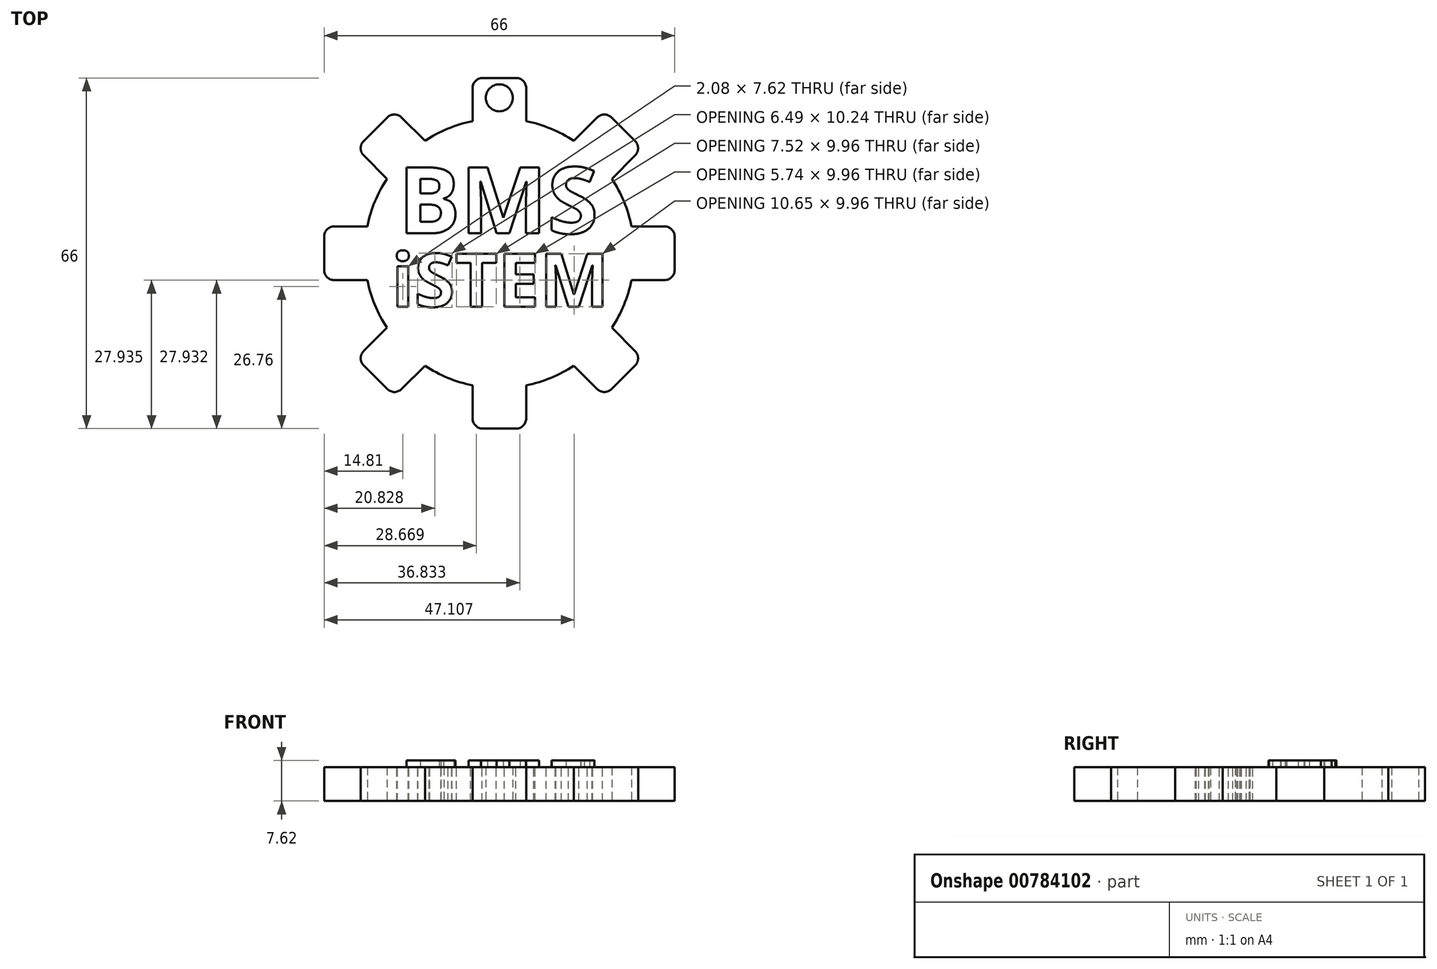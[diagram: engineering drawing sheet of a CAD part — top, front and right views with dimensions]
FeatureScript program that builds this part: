
annotation { "Feature Type Name" : "Feature", "Feature Type Description" : "" }
export const myFeature = defineFeature(function(context is Context, id is Id, definition is map)
    precondition{}
    {
        {
            var Q0;
            Q0=qCreatedBy(makeId("Top.planeOp"),FACE);
            var sketch = newSketch(context, id + "F0", { "sketchPlane" : qUnion([Q0])});
            skCircle(sketch, "E0", {"center": v(0, 0) * mm, "radius": 25.38 * mm});
            skCircle(sketch, "E1.cCircle", {"center": v(0, 0) * mm, "radius": 25.38 * mm, "construction": true});
            skLineSegment(sketch, "E1.0", {"start": v(-5.05, 25.38) * mm, "end": v(5.05, 25.38) * mm});
            skLineSegment(sketch, "E1.1", {"start": v(5.05, 25.38) * mm, "end": v(14.38, 21.52) * mm});
            skLineSegment(sketch, "E1.2", {"start": v(14.38, 21.52) * mm, "end": v(21.52, 14.38) * mm});
            skLineSegment(sketch, "E1.3", {"start": v(21.52, 14.38) * mm, "end": v(25.38, 5.05) * mm});
            skLineSegment(sketch, "E1.4", {"start": v(25.38, 5.05) * mm, "end": v(25.38, -5.05) * mm});
            skLineSegment(sketch, "E1.5", {"start": v(25.38, -5.05) * mm, "end": v(21.52, -14.38) * mm});
            skLineSegment(sketch, "E1.6", {"start": v(21.52, -14.38) * mm, "end": v(14.38, -21.52) * mm});
            skLineSegment(sketch, "E1.7", {"start": v(14.38, -21.52) * mm, "end": v(5.05, -25.38) * mm});
            skLineSegment(sketch, "E1.8", {"start": v(5.05, -25.38) * mm, "end": v(-5.05, -25.38) * mm});
            skLineSegment(sketch, "E1.9", {"start": v(-5.05, -25.38) * mm, "end": v(-14.38, -21.52) * mm});
            skLineSegment(sketch, "E1.10", {"start": v(-14.38, -21.52) * mm, "end": v(-21.52, -14.38) * mm});
            skLineSegment(sketch, "E1.11", {"start": v(-21.52, -14.38) * mm, "end": v(-25.38, -5.05) * mm});
            skLineSegment(sketch, "E1.12", {"start": v(-25.38, -5.05) * mm, "end": v(-25.38, 5.05) * mm});
            skLineSegment(sketch, "E1.13", {"start": v(-25.38, 5.05) * mm, "end": v(-21.52, 14.38) * mm});
            skLineSegment(sketch, "E1.14", {"start": v(-21.52, 14.38) * mm, "end": v(-14.38, 21.52) * mm});
            skLineSegment(sketch, "E1.15", {"start": v(-14.38, 21.52) * mm, "end": v(-5.05, 25.38) * mm});
            skPoint(sketch, "E1.0.midPoint", {"position": v(0, 25.38) * mm});
            skLineSegment(sketch, "E2", {"start": v(-5.05, 25.38) * mm, "end": v(-5.05, 31.1) * mm});
            skLineSegment(sketch, "E3", {"start": v(-3.14, 33) * mm, "end": v(3.14, 33) * mm});
            skLineSegment(sketch, "E4", {"start": v(5.05, 31.1) * mm, "end": v(5.05, 25.38) * mm});
            skLineSegment(sketch, "E5", {"start": v(14.38, 21.52) * mm, "end": v(18.42, 25.56) * mm});
            skLineSegment(sketch, "E6", {"start": v(21.52, 14.38) * mm, "end": v(25.56, 18.42) * mm});
            skLineSegment(sketch, "E7", {"start": v(21.11, 25.56) * mm, "end": v(25.56, 21.11) * mm});
            skLineSegment(sketch, "E8", {"start": v(-14.38, 21.52) * mm, "end": v(-18.42, 25.56) * mm});
            skLineSegment(sketch, "E9", {"start": v(-21.52, 14.38) * mm, "end": v(-25.56, 18.42) * mm});
            skLineSegment(sketch, "E10", {"start": v(-25.56, 21.11) * mm, "end": v(-21.11, 25.56) * mm});
            skLineSegment(sketch, "E11", {"start": v(-25.38, 5.05) * mm, "end": v(-31.1, 5.05) * mm});
            skLineSegment(sketch, "E12", {"start": v(-33, 3.14) * mm, "end": v(-33, -3.14) * mm});
            skLineSegment(sketch, "E13", {"start": v(-31.1, -5.05) * mm, "end": v(-25.38, -5.05) * mm});
            skLineSegment(sketch, "E14", {"start": v(-21.52, -14.38) * mm, "end": v(-25.56, -18.42) * mm});
            skLineSegment(sketch, "E15", {"start": v(-14.38, -21.52) * mm, "end": v(-18.42, -25.56) * mm});
            skLineSegment(sketch, "E16", {"start": v(-21.1, -25.56) * mm, "end": v(-25.56, -21.11) * mm});
            skLineSegment(sketch, "E17", {"start": v(-5.05, -25.38) * mm, "end": v(-5.05, -31.1) * mm});
            skLineSegment(sketch, "E18", {"start": v(-3.14, -33) * mm, "end": v(3.14, -33) * mm});
            skLineSegment(sketch, "E19", {"start": v(5.05, -31.1) * mm, "end": v(5.05, -25.38) * mm});
            skLineSegment(sketch, "E20", {"start": v(14.38, -21.52) * mm, "end": v(18.42, -25.56) * mm});
            skLineSegment(sketch, "E21", {"start": v(21.52, -14.38) * mm, "end": v(25.56, -18.42) * mm});
            skLineSegment(sketch, "E22", {"start": v(25.56, -21.11) * mm, "end": v(21.11, -25.56) * mm});
            skLineSegment(sketch, "E23", {"start": v(25.38, 5.05) * mm, "end": v(31.1, 5.05) * mm});
            skLineSegment(sketch, "E24", {"start": v(25.38, -5.05) * mm, "end": v(31.1, -5.05) * mm});
            skLineSegment(sketch, "E25", {"start": v(33, -3.14) * mm, "end": v(33, 3.14) * mm});
            skPoint(sketch, "E26.visualSharp", {"position": v(-19.77, 26.9) * mm});
            skArc(sketch, "E26.filletArc", {"start": v(-18.42, 25.56) * mm, "mid": v(-19.77, 26.12) * mm, "end": v(-21.11, 25.56) * mm});
            skPoint(sketch, "E27.visualSharp", {"position": v(-26.9, 19.77) * mm});
            skArc(sketch, "E27.filletArc", {"start": v(-25.56, 21.11) * mm, "mid": v(-26.12, 19.77) * mm, "end": v(-25.56, 18.42) * mm});
            skPoint(sketch, "E28.visualSharp", {"position": v(-33, 5.05) * mm});
            skArc(sketch, "E28.filletArc", {"start": v(-31.1, 5.05) * mm, "mid": v(-32.45, 4.5) * mm, "end": v(-33, 3.14) * mm});
            skPoint(sketch, "E29.visualSharp", {"position": v(-33, -5.05) * mm});
            skArc(sketch, "E29.filletArc", {"start": v(-33, -3.14) * mm, "mid": v(-32.45, -4.5) * mm, "end": v(-31.1, -5.05) * mm});
            skPoint(sketch, "E30.visualSharp", {"position": v(-26.9, -19.77) * mm});
            skArc(sketch, "E30.filletArc", {"start": v(-25.56, -18.42) * mm, "mid": v(-26.12, -19.77) * mm, "end": v(-25.56, -21.11) * mm});
            skPoint(sketch, "E31.visualSharp", {"position": v(-19.76, -26.9) * mm});
            skArc(sketch, "E31.filletArc", {"start": v(-21.1, -25.56) * mm, "mid": v(-19.76, -26.11) * mm, "end": v(-18.42, -25.56) * mm});
            skPoint(sketch, "E32.visualSharp", {"position": v(5.05, -33) * mm});
            skArc(sketch, "E32.filletArc", {"start": v(3.14, -33) * mm, "mid": v(4.5, -32.45) * mm, "end": v(5.05, -31.1) * mm});
            skPoint(sketch, "E33.visualSharp", {"position": v(-5.05, -33) * mm});
            skArc(sketch, "E33.filletArc", {"start": v(-5.05, -31.1) * mm, "mid": v(-4.5, -32.45) * mm, "end": v(-3.14, -33) * mm});
            skPoint(sketch, "E34.visualSharp", {"position": v(19.77, -26.9) * mm});
            skArc(sketch, "E34.filletArc", {"start": v(18.42, -25.56) * mm, "mid": v(19.77, -26.12) * mm, "end": v(21.11, -25.56) * mm});
            skPoint(sketch, "E35.visualSharp", {"position": v(26.9, -19.77) * mm});
            skArc(sketch, "E35.filletArc", {"start": v(25.56, -21.11) * mm, "mid": v(26.12, -19.77) * mm, "end": v(25.56, -18.42) * mm});
            skPoint(sketch, "E36.visualSharp", {"position": v(33, -5.05) * mm});
            skArc(sketch, "E36.filletArc", {"start": v(31.1, -5.05) * mm, "mid": v(32.45, -4.5) * mm, "end": v(33, -3.14) * mm});
            skPoint(sketch, "E37.visualSharp", {"position": v(33, 5.05) * mm});
            skArc(sketch, "E37.filletArc", {"start": v(33, 3.14) * mm, "mid": v(32.45, 4.5) * mm, "end": v(31.1, 5.05) * mm});
            skPoint(sketch, "E38.visualSharp", {"position": v(26.9, 19.77) * mm});
            skArc(sketch, "E38.filletArc", {"start": v(25.56, 18.42) * mm, "mid": v(26.12, 19.77) * mm, "end": v(25.56, 21.11) * mm});
            skPoint(sketch, "E39.visualSharp", {"position": v(19.77, 26.9) * mm});
            skArc(sketch, "E39.filletArc", {"start": v(21.11, 25.56) * mm, "mid": v(19.77, 26.12) * mm, "end": v(18.42, 25.56) * mm});
            skPoint(sketch, "E40.visualSharp", {"position": v(5.05, 33) * mm});
            skArc(sketch, "E40.filletArc", {"start": v(5.05, 31.1) * mm, "mid": v(4.5, 32.45) * mm, "end": v(3.14, 33) * mm});
            skPoint(sketch, "E41.visualSharp", {"position": v(-5.05, 33) * mm});
            skArc(sketch, "E41.filletArc", {"start": v(-3.14, 33) * mm, "mid": v(-4.5, 32.45) * mm, "end": v(-5.05, 31.1) * mm});
            skLineSegment(sketch, "E42", {"start": v(-5.05, 25.38) * mm, "end": v(-5.05, 24.88) * mm});
            skLineSegment(sketch, "E43", {"start": v(5.05, 25.38) * mm, "end": v(5.05, 24.88) * mm});
            skLineSegment(sketch, "E44", {"start": v(14.38, 21.52) * mm, "end": v(14.02, 21.16) * mm});
            skLineSegment(sketch, "E45", {"start": v(21.52, 14.38) * mm, "end": v(21.16, 14.02) * mm});
            skLineSegment(sketch, "E46", {"start": v(25.38, 5.05) * mm, "end": v(24.88, 5.05) * mm});
            skLineSegment(sketch, "E47", {"start": v(25.38, -5.05) * mm, "end": v(24.88, -5.05) * mm});
            skLineSegment(sketch, "E48", {"start": v(21.52, -14.38) * mm, "end": v(21.16, -14.02) * mm});
            skLineSegment(sketch, "E49", {"start": v(14.38, -21.52) * mm, "end": v(14.02, -21.16) * mm});
            skLineSegment(sketch, "E50", {"start": v(5.05, -25.38) * mm, "end": v(5.05, -24.88) * mm});
            skLineSegment(sketch, "E51", {"start": v(-5.05, -25.38) * mm, "end": v(-5.05, -24.88) * mm});
            skLineSegment(sketch, "E52", {"start": v(-14.38, -21.52) * mm, "end": v(-14.02, -21.16) * mm});
            skLineSegment(sketch, "E53", {"start": v(-21.52, -14.38) * mm, "end": v(-21.16, -14.02) * mm});
            skLineSegment(sketch, "E54", {"start": v(-25.38, -5.05) * mm, "end": v(-24.88, -5.05) * mm});
            skLineSegment(sketch, "E55", {"start": v(-25.38, 5.05) * mm, "end": v(-24.88, 5.05) * mm});
            skLineSegment(sketch, "E56", {"start": v(-21.52, 14.38) * mm, "end": v(-21.16, 14.02) * mm});
            skLineSegment(sketch, "E57", {"start": v(-14.38, 21.52) * mm, "end": v(-14.02, 21.16) * mm});
            skCircle(sketch, "E58", {"center": v(0, 29.27) * mm, "radius": 2.54 * mm});
            skSolve(sketch);
        }
        {
            var Q0;
            {var subQ3=sQuery(id+"F0.wireOp",EDGE,"E8");Q0=makeQuery(id+"F0.imprint","IMPRINT",FACE,{"disambiguationData":[TD([[makeQuery(id+"F0.imprint","IMPRINT",EDGE,{"derivedFrom":subQ3}),1.0]])]});}
            var Q1;
            {var subQ0=sQuery(id+"F0.wireOp",EDGE,"E2");Q1=makeQuery(id+"F0.imprint","IMPRINT",FACE,{"disambiguationData":[TD([[makeQuery(id+"F0.imprint","IMPRINT",EDGE,{"derivedFrom":subQ0}),-1.0]])]});}
            var Q2;
            {var subQ1=sQuery(id+"F0.wireOp",EDGE,"E5");Q2=makeQuery(id+"F0.imprint","IMPRINT",FACE,{"disambiguationData":[TD([[makeQuery(id+"F0.imprint","IMPRINT",EDGE,{"derivedFrom":subQ1}),-1.0]])]});}
            var Q3;
            {var subQ3=sQuery(id+"F0.wireOp",EDGE,"E23");Q3=makeQuery(id+"F0.imprint","IMPRINT",FACE,{"disambiguationData":[TD([[makeQuery(id+"F0.imprint","IMPRINT",EDGE,{"derivedFrom":subQ3}),-1.0]])]});}
            var Q4;
            {var subQ1=sQuery(id+"F0.wireOp",EDGE,"E20");Q4=makeQuery(id+"F0.imprint","IMPRINT",FACE,{"disambiguationData":[TD([[makeQuery(id+"F0.imprint","IMPRINT",EDGE,{"derivedFrom":subQ1}),1.0]])]});}
            var Q5;
            {var subQ0=sQuery(id+"F0.wireOp",EDGE,"E17");Q5=makeQuery(id+"F0.imprint","IMPRINT",FACE,{"disambiguationData":[TD([[makeQuery(id+"F0.imprint","IMPRINT",EDGE,{"derivedFrom":subQ0}),1.0]])]});}
            var Q6;
            {var subQ0=sQuery(id+"F0.wireOp",EDGE,"E14");Q6=makeQuery(id+"F0.imprint","IMPRINT",FACE,{"disambiguationData":[TD([[makeQuery(id+"F0.imprint","IMPRINT",EDGE,{"derivedFrom":subQ0}),1.0]])]});}
            var Q7;
            {var subQ0=sQuery(id+"F0.wireOp",EDGE,"E11");Q7=makeQuery(id+"F0.imprint","IMPRINT",FACE,{"disambiguationData":[TD([[makeQuery(id+"F0.imprint","IMPRINT",EDGE,{"derivedFrom":subQ0}),1.0]])]});}
            var Q8;
            {var subQ0=sQuery(id+"F0.wireOp",EDGE,"E42");Q8=makeQuery(id+"F0.imprint","IMPRINT",FACE,{"disambiguationData":[TD([[makeQuery(id+"F0.imprint","IMPRINT",EDGE,{"derivedFrom":subQ0}),1.0]])]});}
            var Q9;
            {var subQ0=sQuery(id+"F0.wireOp",EDGE,"E43");Q9=makeQuery(id+"F0.imprint","IMPRINT",FACE,{"disambiguationData":[TD([[makeQuery(id+"F0.imprint","IMPRINT",EDGE,{"derivedFrom":subQ0}),-1.0]])]});}
            var Q10;
            {var subQ0=sQuery(id+"F0.wireOp",EDGE,"E44");Q10=makeQuery(id+"F0.imprint","IMPRINT",FACE,{"disambiguationData":[TD([[makeQuery(id+"F0.imprint","IMPRINT",EDGE,{"derivedFrom":subQ0}),1.0]])]});}
            var Q11;
            {var subQ0=sQuery(id+"F0.wireOp",EDGE,"E45");Q11=makeQuery(id+"F0.imprint","IMPRINT",FACE,{"disambiguationData":[TD([[makeQuery(id+"F0.imprint","IMPRINT",EDGE,{"derivedFrom":subQ0}),-1.0]])]});}
            var Q12;
            {var subQ0=sQuery(id+"F0.wireOp",EDGE,"E46");Q12=makeQuery(id+"F0.imprint","IMPRINT",FACE,{"disambiguationData":[TD([[makeQuery(id+"F0.imprint","IMPRINT",EDGE,{"derivedFrom":subQ0}),1.0]])]});}
            var Q13;
            {var subQ0=sQuery(id+"F0.wireOp",EDGE,"E47");Q13=makeQuery(id+"F0.imprint","IMPRINT",FACE,{"disambiguationData":[TD([[makeQuery(id+"F0.imprint","IMPRINT",EDGE,{"derivedFrom":subQ0}),-1.0]])]});}
            var Q14;
            {var subQ0=sQuery(id+"F0.wireOp",EDGE,"E48");Q14=makeQuery(id+"F0.imprint","IMPRINT",FACE,{"disambiguationData":[TD([[makeQuery(id+"F0.imprint","IMPRINT",EDGE,{"derivedFrom":subQ0}),1.0]])]});}
            var Q15;
            {var subQ0=sQuery(id+"F0.wireOp",EDGE,"E49");Q15=makeQuery(id+"F0.imprint","IMPRINT",FACE,{"disambiguationData":[TD([[makeQuery(id+"F0.imprint","IMPRINT",EDGE,{"derivedFrom":subQ0}),-1.0]])]});}
            var Q16;
            {var subQ0=sQuery(id+"F0.wireOp",EDGE,"E51");Q16=makeQuery(id+"F0.imprint","IMPRINT",FACE,{"disambiguationData":[TD([[makeQuery(id+"F0.imprint","IMPRINT",EDGE,{"derivedFrom":subQ0}),-1.0]])]});}
            var Q17;
            {var subQ0=sQuery(id+"F0.wireOp",EDGE,"E50");Q17=makeQuery(id+"F0.imprint","IMPRINT",FACE,{"disambiguationData":[TD([[makeQuery(id+"F0.imprint","IMPRINT",EDGE,{"derivedFrom":subQ0}),1.0]])]});}
            var Q18;
            {var subQ0=sQuery(id+"F0.wireOp",EDGE,"E0");var subQ17=makeQuery(id+"F0.imprint","INTERSECT",VERTEX,{"derivedFrom":[subQ0,sQuery(id+"F0.wireOp",EDGE,"E46")]});Q18=makeQuery(id+"F0.imprint","IMPRINT",FACE,{"disambiguationData":[TD([[makeQuery(id+"F0.imprint","IMPRINT",EDGE,{"disambiguationData":[TD([[subQ17,1.0]])],"derivedFrom":subQ0}),1.0]])]});}
            var Q19;
            {var subQ0=sQuery(id+"F0.wireOp",EDGE,"E52");Q19=makeQuery(id+"F0.imprint","IMPRINT",FACE,{"disambiguationData":[TD([[makeQuery(id+"F0.imprint","IMPRINT",EDGE,{"derivedFrom":subQ0}),1.0]])]});}
            var Q20;
            {var subQ0=sQuery(id+"F0.wireOp",EDGE,"E53");Q20=makeQuery(id+"F0.imprint","IMPRINT",FACE,{"disambiguationData":[TD([[makeQuery(id+"F0.imprint","IMPRINT",EDGE,{"derivedFrom":subQ0}),-1.0]])]});}
            var Q21;
            {var subQ0=sQuery(id+"F0.wireOp",EDGE,"E54");Q21=makeQuery(id+"F0.imprint","IMPRINT",FACE,{"disambiguationData":[TD([[makeQuery(id+"F0.imprint","IMPRINT",EDGE,{"derivedFrom":subQ0}),1.0]])]});}
            var Q22;
            {var subQ0=sQuery(id+"F0.wireOp",EDGE,"E55");Q22=makeQuery(id+"F0.imprint","IMPRINT",FACE,{"disambiguationData":[TD([[makeQuery(id+"F0.imprint","IMPRINT",EDGE,{"derivedFrom":subQ0}),-1.0]])]});}
            var Q23;
            {var subQ0=sQuery(id+"F0.wireOp",EDGE,"E56");Q23=makeQuery(id+"F0.imprint","IMPRINT",FACE,{"disambiguationData":[TD([[makeQuery(id+"F0.imprint","IMPRINT",EDGE,{"derivedFrom":subQ0}),1.0]])]});}
            var Q24;
            {var subQ0=sQuery(id+"F0.wireOp",EDGE,"E57");Q24=makeQuery(id+"F0.imprint","IMPRINT",FACE,{"disambiguationData":[TD([[makeQuery(id+"F0.imprint","IMPRINT",EDGE,{"derivedFrom":subQ0}),-1.0]])]});}
            extrude(context, id + "F1", {"entities" : qUnion([Q0, Q1, Q2, Q3, Q4, Q5, Q6, Q7, Q8, Q9, Q10, Q11, Q12, Q13, Q14, Q15, Q16, Q17, Q18, Q19, Q20, Q21, Q22, Q23, Q24]), "depth" : 6.35 * mm, "offsetDistance" : 25.4 * mm});
        }
        {
            var Q0;
            Q0=makeQuery(id+"F1.opExtrude","CAP_FACE",FACE,{"disambiguationData":[OSD([sQuery(id+"F0.wireOp",EDGE,"E1.1"),sQuery(id+"F0.wireOp",EDGE,"E1.3"),sQuery(id+"F0.wireOp",EDGE,"E1.5"),sQuery(id+"F0.wireOp",EDGE,"E1.7"),sQuery(id+"F0.wireOp",EDGE,"E1.9"),sQuery(id+"F0.wireOp",EDGE,"E1.11"),sQuery(id+"F0.wireOp",EDGE,"E1.13"),sQuery(id+"F0.wireOp",EDGE,"E1.15"),sQuery(id+"F0.wireOp",EDGE,"E2"),sQuery(id+"F0.wireOp",EDGE,"E3"),sQuery(id+"F0.wireOp",EDGE,"E4"),sQuery(id+"F0.wireOp",EDGE,"E5"),sQuery(id+"F0.wireOp",EDGE,"E6"),sQuery(id+"F0.wireOp",EDGE,"E7"),sQuery(id+"F0.wireOp",EDGE,"E8"),sQuery(id+"F0.wireOp",EDGE,"E9"),sQuery(id+"F0.wireOp",EDGE,"E10"),sQuery(id+"F0.wireOp",EDGE,"E11"),sQuery(id+"F0.wireOp",EDGE,"E12"),sQuery(id+"F0.wireOp",EDGE,"E13"),sQuery(id+"F0.wireOp",EDGE,"E14"),sQuery(id+"F0.wireOp",EDGE,"E15"),sQuery(id+"F0.wireOp",EDGE,"E16"),sQuery(id+"F0.wireOp",EDGE,"E17"),sQuery(id+"F0.wireOp",EDGE,"E18"),sQuery(id+"F0.wireOp",EDGE,"E19"),sQuery(id+"F0.wireOp",EDGE,"E20"),sQuery(id+"F0.wireOp",EDGE,"E21"),sQuery(id+"F0.wireOp",EDGE,"E22"),sQuery(id+"F0.wireOp",EDGE,"E23"),sQuery(id+"F0.wireOp",EDGE,"E24"),sQuery(id+"F0.wireOp",EDGE,"E25")])],"isStart":false});
            var sketch = newSketch(context, id + "F2", { "sketchPlane" : qUnion([Q0])});
            skText(sketch, "E59", { "text": "iSTEM", "fontName": "OpenSans-Bold.ttf"});
            const initialGuessF2  = {"E59": [-0.02032, -0.01005, 1, 0, 0.01005]};
            skSetInitialGuess(sketch, initialGuessF2);
            skSolve(sketch);
        }
        {
            var Q0;
            Q0 = qSketchRegion(id + "F2", true);
            var Q1;
            Q1=makeQuery(id+"F6ugocPZYVqLwCi_1.imprint","IMPRINT",FACE,{"disambiguationData":[TD([[makeQuery(id+"F6ugocPZYVqLwCi_1.imprint","IMPRINT",EDGE,{"derivedFrom":makeQuery(id+"F2.imprint","IMPRINT",EDGE,{"derivedFrom":sQuery(id+"F2.wireOp",EDGE,"238f4873-60e4-4737-845d-4de3b97efb3e.sketch_text.stroke-32")})}),-1.0]])]});
            extrude(context, id + "F3", {"entities" : qUnion([Q0, Q1]), "operationType" : NewBodyOperationType.REMOVE, "oppositeDirection" : true, "depth" : 42.93 * mm, "offsetDistance" : 25.4 * mm});
        }
        {
            var Q0;
            Q0=makeQuery(id+"F1.opExtrude","CAP_FACE",FACE,{"disambiguationData":[OSD([sQuery(id+"F0.wireOp",EDGE,"E0"),sQuery(id+"F0.wireOp",EDGE,"E2"),sQuery(id+"F0.wireOp",EDGE,"E3"),sQuery(id+"F0.wireOp",EDGE,"E4"),sQuery(id+"F0.wireOp",EDGE,"E5"),sQuery(id+"F0.wireOp",EDGE,"E6"),sQuery(id+"F0.wireOp",EDGE,"E7"),sQuery(id+"F0.wireOp",EDGE,"E8"),sQuery(id+"F0.wireOp",EDGE,"E9"),sQuery(id+"F0.wireOp",EDGE,"E10"),sQuery(id+"F0.wireOp",EDGE,"E11"),sQuery(id+"F0.wireOp",EDGE,"E12"),sQuery(id+"F0.wireOp",EDGE,"E13"),sQuery(id+"F0.wireOp",EDGE,"E14"),sQuery(id+"F0.wireOp",EDGE,"E15"),sQuery(id+"F0.wireOp",EDGE,"E16"),sQuery(id+"F0.wireOp",EDGE,"E17"),sQuery(id+"F0.wireOp",EDGE,"E18"),sQuery(id+"F0.wireOp",EDGE,"E19"),sQuery(id+"F0.wireOp",EDGE,"E20"),sQuery(id+"F0.wireOp",EDGE,"E21"),sQuery(id+"F0.wireOp",EDGE,"E22"),sQuery(id+"F0.wireOp",EDGE,"E23"),sQuery(id+"F0.wireOp",EDGE,"E24"),sQuery(id+"F0.wireOp",EDGE,"E25"),sQuery(id+"F0.wireOp",EDGE,"E26.filletArc"),sQuery(id+"F0.wireOp",EDGE,"E27.filletArc"),sQuery(id+"F0.wireOp",EDGE,"E28.filletArc"),sQuery(id+"F0.wireOp",EDGE,"E29.filletArc"),sQuery(id+"F0.wireOp",EDGE,"E30.filletArc"),sQuery(id+"F0.wireOp",EDGE,"E31.filletArc"),sQuery(id+"F0.wireOp",EDGE,"E32.filletArc"),sQuery(id+"F0.wireOp",EDGE,"E33.filletArc"),sQuery(id+"F0.wireOp",EDGE,"E34.filletArc"),sQuery(id+"F0.wireOp",EDGE,"E35.filletArc"),sQuery(id+"F0.wireOp",EDGE,"E36.filletArc"),sQuery(id+"F0.wireOp",EDGE,"E37.filletArc"),sQuery(id+"F0.wireOp",EDGE,"E38.filletArc"),sQuery(id+"F0.wireOp",EDGE,"E39.filletArc"),sQuery(id+"F0.wireOp",EDGE,"E40.filletArc"),sQuery(id+"F0.wireOp",EDGE,"E41.filletArc"),sQuery(id+"F0.wireOp",EDGE,"E42"),sQuery(id+"F0.wireOp",EDGE,"E43"),sQuery(id+"F0.wireOp",EDGE,"E44"),sQuery(id+"F0.wireOp",EDGE,"E45"),sQuery(id+"F0.wireOp",EDGE,"E46"),sQuery(id+"F0.wireOp",EDGE,"E47"),sQuery(id+"F0.wireOp",EDGE,"E48"),sQuery(id+"F0.wireOp",EDGE,"E49"),sQuery(id+"F0.wireOp",EDGE,"E50"),sQuery(id+"F0.wireOp",EDGE,"E51"),sQuery(id+"F0.wireOp",EDGE,"E52"),sQuery(id+"F0.wireOp",EDGE,"E53"),sQuery(id+"F0.wireOp",EDGE,"E54"),sQuery(id+"F0.wireOp",EDGE,"E55"),sQuery(id+"F0.wireOp",EDGE,"E56"),sQuery(id+"F0.wireOp",EDGE,"E57"),sQuery(id+"F0.wireOp",EDGE,"E58")])],"isStart":false});
            var sketch = newSketch(context, id + "F4", { "sketchPlane" : qUnion([Q0])});
            skText(sketch, "E60", { "text": "BMS", "fontName": "OpenSans-Bold.ttf"});
            const initialGuessF4  = {"E60": [-0.01905, 0.00375, 1, 0, 0.01252]};
            skSetInitialGuess(sketch, initialGuessF4);
            skSolve(sketch);
        }
        {
            var Q0;
            Q0 = qSketchRegion(id + "F4", true);
            extrude(context, id + "F5", {"entities" : qUnion([Q0]), "operationType" : NewBodyOperationType.ADD, "depth" : 1.27 * mm, "offsetDistance" : 25.4 * mm});
        }
    });
